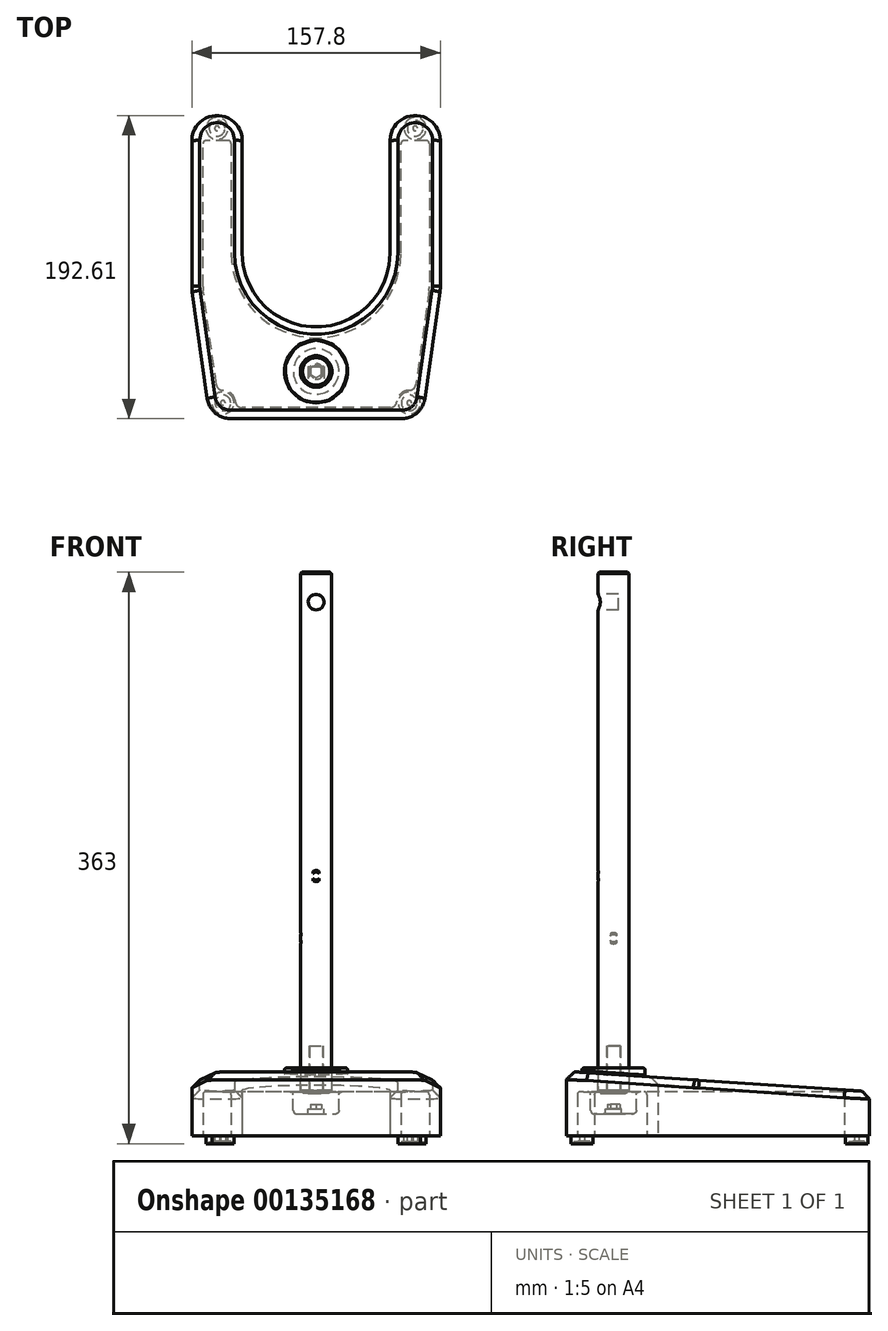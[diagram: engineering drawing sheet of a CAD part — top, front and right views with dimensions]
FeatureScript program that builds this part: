
annotation { "Feature Type Name" : "Feature", "Feature Type Description" : "" }
export const myFeature = defineFeature(function(context is Context, id is Id, definition is map)
    precondition{}
    {
        {
            var Q0;
            Q0=qCreatedBy(makeId("Top.planeOp"),FACE);
            var sketch = newSketch(context, id + "F0", { "sketchPlane" : qUnion([Q0])});
            skLineSegment(sketch, "E0", {"start": v(0, 0) * mm, "end": v(-54.3, 0) * mm});
            skLineSegment(sketch, "E1", {"start": v(-54.3, 0) * mm, "end": v(-54.3, 15) * mm, "construction": true});
            skArc(sketch, "E2", {"start": v(-69.15, 12.91) * mm, "mid": v(-64.14, 3.68) * mm, "end": v(-54.3, 0) * mm});
            skLineSegment(sketch, "E3", {"start": v(-69.15, 12.91) * mm, "end": v(-78.66, 80.53) * mm});
            skLineSegment(sketch, "E4", {"start": v(-78.9, 84) * mm, "end": v(-78.9, 176.6) * mm});
            skPoint(sketch, "E5.visualSharp", {"position": v(-78.9, 82.26) * mm});
            skArc(sketch, "E5.filletArc", {"start": v(-78.9, 84) * mm, "mid": v(-78.84, 82.26) * mm, "end": v(-78.66, 80.53) * mm});
            skLineSegment(sketch, "E6", {"start": v(-78.9, 176.6) * mm, "end": v(-62.9, 176.6) * mm, "construction": true});
            skArc(sketch, "E7", {"start": v(-46.9, 176.6) * mm, "mid": v(-62.9, 192.6) * mm, "end": v(-78.9, 176.6) * mm});
            skLineSegment(sketch, "E8", {"start": v(-46.9, 176.6) * mm, "end": v(-46.9, 105.2) * mm});
            skLineSegment(sketch, "E9", {"start": v(0, 58.3) * mm, "end": v(0, 192.6) * mm, "construction": true});
            skPoint(sketch, "E9.endSnap0", {"position": v(-62.9, 192.6) * mm});
            skArc(sketch, "E10", {"start": v(-46.9, 105.2) * mm, "mid": v(-33.16, 72.04) * mm, "end": v(0, 58.3) * mm});
            skLineSegment(sketch, "E11", {"start": v(0, 58.3) * mm, "end": v(0, 0) * mm});
            skSolve(sketch);
        }
        {
            var Q0;
            Q0=qSketchRegion(id+"F0",true);
            extrude(context, id + "F1", {"entities" : qUnion([Q0]), "depth" : 41 * mm});
        }
        {
            var Q0;
            Q0=makeQuery(id+"F1.opExtrude","SWEPT_BODY",BODY,{"disambiguationData":[OSD([sQuery(id+"F0.wireOp",EDGE,"E0"),sQuery(id+"F0.wireOp",EDGE,"E2"),sQuery(id+"F0.wireOp",EDGE,"E3"),sQuery(id+"F0.wireOp",EDGE,"E4"),sQuery(id+"F0.wireOp",EDGE,"E5.filletArc"),sQuery(id+"F0.wireOp",EDGE,"E7"),sQuery(id+"F0.wireOp",EDGE,"E8"),sQuery(id+"F0.wireOp",EDGE,"E10"),sQuery(id+"F0.wireOp",EDGE,"E11")])]});
            var Q1;
            Q1=qCreatedBy(makeId("Right.planeOp"),FACE);
            mirror(context, id + "F2", {"operationType" : NewBodyOperationType.ADD, "entities" : qUnion([Q0]), "mirrorPlane" : qUnion([Q1])});
        }
        {
            var Q0;
            Q0=qCreatedBy(makeId("Right.planeOp"),FACE);
            var sketch = newSketch(context, id + "F3", { "sketchPlane" : qUnion([Q0])});
            skLineSegment(sketch, "E12", {"start": v(0, 0) * mm, "end": v(0, 18) * mm, "construction": true});
            skPoint(sketch, "E13.0", {"position": v(0, 41) * mm});
            skLineSegment(sketch, "E14", {"start": v(0, 41) * mm, "end": v(5, 41) * mm});
            skLineSegment(sketch, "E15", {"start": v(0, 18) * mm, "end": v(192.61, 18) * mm});
            skLineSegment(sketch, "E16", {"start": v(192.61, 18) * mm, "end": v(192.61, 28) * mm, "construction": true});
            skLineSegment(sketch, "E17", {"start": v(192.61, 28) * mm, "end": v(187.6, 28) * mm});
            skLineSegment(sketch, "E18", {"start": v(192.61, 41) * mm, "end": v(192.61, 28) * mm});
            skLineSegment(sketch, "E19", {"start": v(0, 18) * mm, "end": v(0, 41) * mm});
            skLineSegment(sketch, "E20", {"start": v(5, 18) * mm, "end": v(0, 18) * mm});
            skLineSegment(sketch, "E21", {"start": v(0, 41) * mm, "end": v(192.61, 28) * mm});
            skLineSegment(sketch, "E22", {"start": v(192.61, 41) * mm, "end": v(0, 41) * mm});
            skSolve(sketch);
        }
        {
            var Q0;
            {var subQ0=sQuery(id+"F3.wireOp",EDGE,"E18");Q0=makeQuery(id+"F3.imprint","IMPRINT",FACE,{"disambiguationData":[TD([[makeQuery(id+"F3.imprint","IMPRINT",EDGE,{"derivedFrom":subQ0}),-1.0]])]});}
            extrude(context, id + "F4", {"entities" : qUnion([Q0]), "operationType" : NewBodyOperationType.REMOVE, "endBound" : BoundingType.THROUGH_ALL, "oppositeDirection" : true, "depth" : 25 * mm, "hasSecondDirection" : true, "secondDirectionBound" : SecondDirectionBoundingType.THROUGH_ALL, "secondDirectionOppositeDirection" : false, "secondDirectionDepth" : 25 * mm});
        }
        {
            var Q0;
            Q0=makeQuery(id+"F4.boolean.opBoolean","INTERSECT",EDGE,{"derivedFrom":[makeQuery(id+"F1.opExtrude","SWEPT_FACE",FACE,{"disambiguationData":[OSD([sQuery(id+"F0.wireOp",EDGE,"E4")])]}),makeQuery(id+"F4.opExtrude","SWEPT_FACE",FACE,{"disambiguationData":[OSD([sQuery(id+"F3.wireOp",EDGE,"E21")])]})]});
            chamfer(context, id + "F5", {"entities" : qUnion([Q0]), "width" : 5 * mm, "tangentPropagation" : true});
        }
        {
            var Q0;
            Q0=qCreatedBy(makeId("Front.planeOp"),FACE);
            var sketch = newSketch(context, id + "F6", { "sketchPlane" : qUnion([Q0])});
            skLineSegment(sketch, "E23", {"start": v(0, 0) * mm, "end": v(0, 44) * mm, "construction": true});
            skSolve(sketch);
        }
        {
            var Q0;
            Q0=qCreatedBy(makeId("Right.planeOp"),FACE);
            var sketch = newSketch(context, id + "F7", { "sketchPlane" : qUnion([Q0])});
            skLineSegment(sketch, "E24.0", {"start": v(0, 0) * mm, "end": v(0, 44) * mm, "construction": true});
            skLineSegment(sketch, "E25", {"start": v(0, 44) * mm, "end": v(30, 44) * mm, "construction": true});
            skSolve(sketch);
        }
        {
            var Q0;
            Q0=qCreatedBy(makeId("Top.planeOp"),FACE);
            var sketch = newSketch(context, id + "F8", { "sketchPlane" : qUnion([Q0])});
            skLineSegment(sketch, "E26.0", {"start": v(0, 0) * mm, "end": v(0, 30) * mm});
            skCircle(sketch, "E27", {"center": v(0, 30) * mm, "radius": 20 * mm});
            skSolve(sketch);
        }
        {
            var Q0;
            Q0=qSketchRegion(id+"F8",true);
            extrude(context, id + "F9", {"entities" : qUnion([Q0]), "operationType" : NewBodyOperationType.ADD, "depth" : 43 * mm});
        }
        {
            var Q0;
            Q0=makeQuery(id+"F9.opExtrude","CAP_FACE",FACE,{"disambiguationData":[OSD([sQuery(id+"F8.wireOp",EDGE,"E27")])],"isStart":false});
            var sketch = newSketch(context, id + "F10", { "sketchPlane" : qUnion([Q0])});
            skCircle(sketch, "E28", {"center": v(0, 30) * mm, "radius": 10 * mm});
            skSolve(sketch);
        }
        {
            var Q0;
            Q0=qSketchRegion(id+"F10",true);
            extrude(context, id + "F11", {"entities" : qUnion([Q0]), "operationType" : NewBodyOperationType.REMOVE, "oppositeDirection" : true, "depth" : 18 * mm});
        }
        {
            var Q0;
            Q0=makeQuery(id+"F11.boolean.opBoolean","COPY",FACE,{"derivedFrom":makeQuery(id+"F11.opExtrude","CAP_FACE",FACE,{"disambiguationData":[OSD([sQuery(id+"F10.wireOp",EDGE,"E28")])],"isStart":false})});
            var sketch = newSketch(context, id + "F12", { "sketchPlane" : qUnion([Q0])});
            skCircle(sketch, "E29", {"center": v(0, 30) * mm, "radius": 5 * mm});
            skSolve(sketch);
        }
        {
            var Q0;
            Q0=qSketchRegion(id+"F12",true);
            extrude(context, id + "F13", {"entities" : qUnion([Q0]), "operationType" : NewBodyOperationType.REMOVE, "endBound" : BoundingType.THROUGH_ALL, "oppositeDirection" : true, "depth" : 25 * mm});
        }
        {
            var Q0;
            {var subQ0=makeQuery(id+"F1.opExtrude","CAP_FACE",FACE,{"disambiguationData":[OSD([sQuery(id+"F0.wireOp",EDGE,"E0"),sQuery(id+"F0.wireOp",EDGE,"E2"),sQuery(id+"F0.wireOp",EDGE,"E3"),sQuery(id+"F0.wireOp",EDGE,"E4"),sQuery(id+"F0.wireOp",EDGE,"E5.filletArc"),sQuery(id+"F0.wireOp",EDGE,"E7"),sQuery(id+"F0.wireOp",EDGE,"E8"),sQuery(id+"F0.wireOp",EDGE,"E10"),sQuery(id+"F0.wireOp",EDGE,"E11")])],"isStart":true});Q0=makeQuery(id+"F2.boolean.opBoolean","MERGE",FACE,{"derivedFrom":[subQ0,makeQuery(id+"F2.opPattern","COPY",FACE,{"derivedFrom":subQ0,"instanceName":"1"})]});}
            var sketch = newSketch(context, id + "F14", { "sketchPlane" : qUnion([Q0])});
            skLineSegment(sketch, "E30.1", {"start": v(71.72, -81.5) * mm, "end": v(63.28, -21.44) * mm});
            skArc(sketch, "E30.2", {"start": v(71.9, -84) * mm, "mid": v(71.86, -82.75) * mm, "end": v(71.72, -81.5) * mm});
            skLineSegment(sketch, "E30.3", {"start": v(-71.9, -84) * mm, "end": v(-71.9, -174.6) * mm});
            skArc(sketch, "E30.4", {"start": v(-71.72, -81.5) * mm, "mid": v(-71.86, -82.75) * mm, "end": v(-71.9, -84) * mm});
            skLineSegment(sketch, "E30.5", {"start": v(-63, -19.44) * mm, "end": v(-71.72, -81.5) * mm});
            skLineSegment(sketch, "E30.8", {"start": v(-53.9, -174.6) * mm, "end": v(-53.9, -105.2) * mm});
            skArc(sketch, "E30.9", {"start": v(-53.9, -105.2) * mm, "mid": v(0, -51.3) * mm, "end": v(53.9, -105.2) * mm});
            skLineSegment(sketch, "E30.10", {"start": v(47.2, -7) * mm, "end": v(-47.2, -7) * mm});
            skLineSegment(sketch, "E30.11", {"start": v(53.9, -105.2) * mm, "end": v(53.9, -174.6) * mm});
            skLineSegment(sketch, "E30.13", {"start": v(71.9, -174.6) * mm, "end": v(71.9, -84) * mm});
            skLineSegment(sketch, "E31", {"start": v(69.9, -176.6) * mm, "end": v(55.9, -176.6) * mm});
            skLineSegment(sketch, "E32", {"start": v(-55.9, -176.6) * mm, "end": v(-69.9, -176.6) * mm});
            skPoint(sketch, "E33.visualSharp", {"position": v(71.9, -176.6) * mm});
            skArc(sketch, "E33.filletArc", {"start": v(69.9, -176.6) * mm, "mid": v(71.31, -176.02) * mm, "end": v(71.9, -174.6) * mm});
            skPoint(sketch, "E34.visualSharp", {"position": v(53.9, -176.6) * mm});
            skArc(sketch, "E34.filletArc", {"start": v(53.9, -174.6) * mm, "mid": v(54.49, -176.02) * mm, "end": v(55.9, -176.6) * mm});
            skPoint(sketch, "E35.visualSharp", {"position": v(-53.9, -176.6) * mm});
            skArc(sketch, "E35.filletArc", {"start": v(-55.9, -176.6) * mm, "mid": v(-54.49, -176.02) * mm, "end": v(-53.9, -174.6) * mm});
            skPoint(sketch, "E36.visualSharp", {"position": v(-71.9, -176.6) * mm});
            skArc(sketch, "E36.filletArc", {"start": v(-71.9, -174.6) * mm, "mid": v(-71.31, -176.02) * mm, "end": v(-69.9, -176.6) * mm});
            skArc(sketch, "E37", {"start": v(51.18, -10.67) * mm, "mid": v(53.78, -15.93) * mm, "end": v(59.27, -18) * mm});
            skPoint(sketch, "E38.visualSharp", {"position": v(51.74, -7) * mm});
            skArc(sketch, "E38.filletArc", {"start": v(51.18, -10.67) * mm, "mid": v(49.9, -8.06) * mm, "end": v(47.2, -7) * mm});
            skPoint(sketch, "E39.visualSharp", {"position": v(62.68, -17.18) * mm});
            skArc(sketch, "E39.filletArc", {"start": v(63.28, -21.44) * mm, "mid": v(61.93, -18.96) * mm, "end": v(59.27, -18) * mm});
            skLineSegment(sketch, "E40", {"start": v(0, 0) * mm, "end": v(0, -30) * mm, "construction": true});
            skArc(sketch, "E41.MirrorCS", {"start": v(-63.28, -21.44) * mm, "mid": v(-61.93, -18.96) * mm, "end": v(-59.27, -18) * mm});
            skArc(sketch, "E42.MirrorCS", {"start": v(-51.18, -10.67) * mm, "mid": v(-53.78, -15.93) * mm, "end": v(-59.27, -18) * mm});
            skArc(sketch, "E43.MirrorCS", {"start": v(-51.18, -10.67) * mm, "mid": v(-49.9, -8.06) * mm, "end": v(-47.2, -7) * mm});
            skSolve(sketch);
        }
        {
            var Q0;
            Q0=qSketchRegion(id+"F14",true);
            extrude(context, id + "F15", {"entities" : qUnion([Q0]), "operationType" : NewBodyOperationType.REMOVE, "oppositeDirection" : true, "depth" : 28 * mm});
        }
        {
            var Q0;
            Q0=makeQuery(id+"F15.boolean.opBoolean","COPY",FACE,{"derivedFrom":makeQuery(id+"F15.opExtrude","CAP_FACE",FACE,{"disambiguationData":[OSD([sQuery(id+"F14.wireOp",EDGE,"E30.1"),sQuery(id+"F14.wireOp",EDGE,"E30.2"),sQuery(id+"F14.wireOp",EDGE,"E30.3"),sQuery(id+"F14.wireOp",EDGE,"E30.4"),sQuery(id+"F14.wireOp",EDGE,"E30.5"),sQuery(id+"F14.wireOp",EDGE,"E30.8"),sQuery(id+"F14.wireOp",EDGE,"E30.9"),sQuery(id+"F14.wireOp",EDGE,"E30.10"),sQuery(id+"F14.wireOp",EDGE,"E30.11"),sQuery(id+"F14.wireOp",EDGE,"E30.13"),sQuery(id+"F14.wireOp",EDGE,"E31"),sQuery(id+"F14.wireOp",EDGE,"E32"),sQuery(id+"F14.wireOp",EDGE,"E33.filletArc"),sQuery(id+"F14.wireOp",EDGE,"E34.filletArc"),sQuery(id+"F14.wireOp",EDGE,"E35.filletArc"),sQuery(id+"F14.wireOp",EDGE,"E36.filletArc"),sQuery(id+"F14.wireOp",EDGE,"E37"),sQuery(id+"F14.wireOp",EDGE,"E38.filletArc"),sQuery(id+"F14.wireOp",EDGE,"E39.filletArc"),sQuery(id+"F14.wireOp",EDGE,"E41.MirrorCS"),sQuery(id+"F14.wireOp",EDGE,"E42.MirrorCS"),sQuery(id+"F14.wireOp",EDGE,"E43.MirrorCS")])],"isStart":false})});
            var sketch = newSketch(context, id + "F16", { "sketchPlane" : qUnion([Q0])});
            skCircle(sketch, "E44", {"center": v(0, -30) * mm, "radius": 14.5 * mm});
            skCircle(sketch, "E45", {"center": v(0, -30) * mm, "radius": 5 * mm});
            skSolve(sketch);
        }
        {
            var Q0;
            Q0=qSketchRegion(id+"F16",true);
            extrude(context, id + "F17", {"entities" : qUnion([Q0]), "operationType" : NewBodyOperationType.ADD, "depth" : 14 * mm});
        }
        {
            var Q0;
            {var subQ0=makeQuery(id+"F1.opExtrude","CAP_FACE",FACE,{"disambiguationData":[OSD([sQuery(id+"F0.wireOp",EDGE,"E0"),sQuery(id+"F0.wireOp",EDGE,"E2"),sQuery(id+"F0.wireOp",EDGE,"E3"),sQuery(id+"F0.wireOp",EDGE,"E4"),sQuery(id+"F0.wireOp",EDGE,"E5.filletArc"),sQuery(id+"F0.wireOp",EDGE,"E7"),sQuery(id+"F0.wireOp",EDGE,"E8"),sQuery(id+"F0.wireOp",EDGE,"E10"),sQuery(id+"F0.wireOp",EDGE,"E11")])],"isStart":true});Q0=makeQuery(id+"F2.boolean.opBoolean","MERGE",FACE,{"derivedFrom":[subQ0,makeQuery(id+"F2.opPattern","COPY",FACE,{"derivedFrom":subQ0,"instanceName":"1"})]});}
            var sketch = newSketch(context, id + "F18", { "sketchPlane" : qUnion([Q0])});
            skCircle(sketch, "E46", {"center": v(59.15, -10) * mm, "radius": 7 * mm});
            skCircle(sketch, "E47", {"center": v(62.9, -184.4) * mm, "radius": 7 * mm});
            skPoint(sketch, "E47.centerSnap0", {"position": v(62.9, -192.6) * mm});
            skSolve(sketch);
        }
        {
            var Q0;
            Q0=qSketchRegion(id+"F18",true);
            extrude(context, id + "F19", {"entities" : qUnion([Q0]), "depth" : 5 * mm});
        }
        {
            var Q0;
            Q0=makeQuery(id+"F19.opExtrude","CAP_FACE",FACE,{"disambiguationData":[OSD([sQuery(id+"F18.wireOp",EDGE,"E46")])],"isStart":false});
            var sketch = newSketch(context, id + "F20", { "sketchPlane" : qUnion([Q0])});
            skCircle(sketch, "E48", {"center": v(59.15, -10) * mm, "radius": 5 * mm});
            skSolve(sketch);
        }
        {
            var Q0;
            Q0=qSketchRegion(id+"F20",true);
            extrude(context, id + "F21", {"entities" : qUnion([Q0]), "operationType" : NewBodyOperationType.REMOVE, "oppositeDirection" : true, "depth" : 1.5 * mm});
        }
        {
            var Q0;
            Q0=makeQuery(id+"F21.boolean.opBoolean","COPY",FACE,{"derivedFrom":makeQuery(id+"F21.opExtrude","CAP_FACE",FACE,{"disambiguationData":[OSD([sQuery(id+"F20.wireOp",EDGE,"E48")])],"isStart":false})});
            var sketch = newSketch(context, id + "F22", { "sketchPlane" : qUnion([Q0])});
            skCircle(sketch, "E49.0", {"center": v(59.15, -10) * mm, "radius": 5 * mm, "construction": true});
            skCircle(sketch, "E50", {"center": v(59.15, -10) * mm, "radius": 1.5 * mm});
            skSolve(sketch);
        }
        {
            var Q0;
            Q0=makeQuery(id+"F22.imprint","IMPRINT",FACE,{"disambiguationData":[TD([[makeQuery(id+"F22.imprint","IMPRINT",EDGE,{"derivedFrom":sQuery(id+"F22.wireOp",EDGE,"E50")}),1.0]])]});
            extrude(context, id + "F23", {"entities" : qUnion([Q0]), "operationType" : NewBodyOperationType.REMOVE, "oppositeDirection" : true, "depth" : 3 * mm});
        }
        {
            var Q0;
            Q0=makeQuery(id+"F19.opExtrude","CAP_FACE",FACE,{"disambiguationData":[OSD([sQuery(id+"F18.wireOp",EDGE,"E47")])],"isStart":false});
            var sketch = newSketch(context, id + "F24", { "sketchPlane" : qUnion([Q0])});
            skCircle(sketch, "E51", {"center": v(62.9, -184.4) * mm, "radius": 5 * mm});
            skSolve(sketch);
        }
        {
            var Q0;
            Q0=qSketchRegion(id+"F24",true);
            extrude(context, id + "F25", {"entities" : qUnion([Q0]), "operationType" : NewBodyOperationType.REMOVE, "oppositeDirection" : true, "depth" : 1.5 * mm});
        }
        {
            var Q0;
            Q0=makeQuery(id+"F25.boolean.opBoolean","COPY",FACE,{"derivedFrom":makeQuery(id+"F25.opExtrude","CAP_FACE",FACE,{"disambiguationData":[OSD([sQuery(id+"F24.wireOp",EDGE,"E51")])],"isStart":false})});
            var sketch = newSketch(context, id + "F26", { "sketchPlane" : qUnion([Q0])});
            skCircle(sketch, "E52", {"center": v(62.9, -184.4) * mm, "radius": 1.5 * mm});
            skSolve(sketch);
        }
        {
            var Q0;
            Q0=qSketchRegion(id+"F26",true);
            extrude(context, id + "F27", {"entities" : qUnion([Q0]), "operationType" : NewBodyOperationType.REMOVE, "oppositeDirection" : true, "depth" : 3 * mm});
        }
        {
            var Q0;
            Q0=makeQuery(id+"F19.opExtrude","SWEPT_BODY",BODY,{"disambiguationData":[OSD([sQuery(id+"F18.wireOp",EDGE,"E46")])]});
            var Q1;
            Q1=makeQuery(id+"F19.opExtrude","SWEPT_BODY",BODY,{"disambiguationData":[OSD([sQuery(id+"F18.wireOp",EDGE,"E47")])]});
            var Q2;
            Q2=qCreatedBy(makeId("Right.planeOp"),FACE);
            mirror(context, id + "F28", {"entities" : qUnion([Q0, Q1]), "mirrorPlane" : qUnion([Q2])});
        }
        {
            var Q0;
            Q0=makeQuery(id+"F15.boolean.opBoolean","COPY",FACE,{"derivedFrom":makeQuery(id+"F15.opExtrude","CAP_FACE",FACE,{"disambiguationData":[OSD([sQuery(id+"F14.wireOp",EDGE,"E30.1"),sQuery(id+"F14.wireOp",EDGE,"E30.2"),sQuery(id+"F14.wireOp",EDGE,"E30.3"),sQuery(id+"F14.wireOp",EDGE,"E30.4"),sQuery(id+"F14.wireOp",EDGE,"E30.5"),sQuery(id+"F14.wireOp",EDGE,"E30.8"),sQuery(id+"F14.wireOp",EDGE,"E30.9"),sQuery(id+"F14.wireOp",EDGE,"E30.10"),sQuery(id+"F14.wireOp",EDGE,"E30.11"),sQuery(id+"F14.wireOp",EDGE,"E30.13"),sQuery(id+"F14.wireOp",EDGE,"E31"),sQuery(id+"F14.wireOp",EDGE,"E32"),sQuery(id+"F14.wireOp",EDGE,"E33.filletArc"),sQuery(id+"F14.wireOp",EDGE,"E34.filletArc"),sQuery(id+"F14.wireOp",EDGE,"E35.filletArc"),sQuery(id+"F14.wireOp",EDGE,"E36.filletArc"),sQuery(id+"F14.wireOp",EDGE,"E37"),sQuery(id+"F14.wireOp",EDGE,"E38.filletArc"),sQuery(id+"F14.wireOp",EDGE,"E39.filletArc"),sQuery(id+"F14.wireOp",EDGE,"E41.MirrorCS"),sQuery(id+"F14.wireOp",EDGE,"E42.MirrorCS"),sQuery(id+"F14.wireOp",EDGE,"E43.MirrorCS")])],"isStart":false})});
            var Q1;
            Q1=makeQuery(id+"F17.opExtrude","CAP_EDGE",EDGE,{"disambiguationData":[OSD([sQuery(id+"F16.wireOp",EDGE,"E44")])],"isStart":false});
            fillet(context, id + "F29", {"entities" : qUnion([Q0, Q1]), "radius" : 2 * mm, "tangentPropagation" : true, "allowEdgeOverflow" : false});
        }
        {
            var Q0;
            Q0=makeQuery(id+"F15.boolean.opBoolean","COPY",EDGE,{"derivedFrom":makeQuery(id+"F15.opExtrude","CAP_EDGE",EDGE,{"disambiguationData":[OSD([sQuery(id+"F14.wireOp",EDGE,"E30.1")])],"isStart":true})});
            var Q1;
            Q1=makeQuery(id+"F9.opExtrude","CAP_EDGE",EDGE,{"disambiguationData":[OSD([sQuery(id+"F8.wireOp",EDGE,"E27")])],"isStart":false});
            var Q2;
            Q2=makeQuery(id+"F9.boolean.opBoolean","INTERSECT",EDGE,{"derivedFrom":[makeQuery(id+"F4.boolean.opBoolean","COPY",FACE,{"derivedFrom":makeQuery(id+"F4.opExtrude","SWEPT_FACE",FACE,{"disambiguationData":[OSD([sQuery(id+"F3.wireOp",EDGE,"E21")])]})}),makeQuery(id+"F9.opExtrude","SWEPT_FACE",FACE,{"disambiguationData":[OSD([sQuery(id+"F8.wireOp",EDGE,"E27")])]})]});
            fillet(context, id + "F30", {"entities" : qUnion([Q0, Q1, Q2]), "radius" : 1 * mm, "tangentPropagation" : true, "allowEdgeOverflow" : false});
        }
        {
            var Q0;
            Q0=makeQuery(id+"F17.opExtrude","CAP_FACE",FACE,{"disambiguationData":[OSD([sQuery(id+"F16.wireOp",EDGE,"E44"),sQuery(id+"F16.wireOp",EDGE,"E45")])],"isStart":true});
            var sketch = newSketch(context, id + "F31", { "sketchPlane" : qUnion([Q0])});
            skCircle(sketch, "E53", {"center": v(0, 30) * mm, "radius": 9.8 * mm});
            skSolve(sketch);
        }
        {
            var Q0;
            Q0=qSketchRegion(id+"F31",true);
            extrude(context, id + "F32", {"entities" : qUnion([Q0]), "depth" : 330 * mm});
        }
        {
            var Q0;
            Q0=makeQuery(id+"F32.opExtrude","CAP_FACE",FACE,{"disambiguationData":[OSD([sQuery(id+"F31.wireOp",EDGE,"E53")])],"isStart":true});
            var sketch = newSketch(context, id + "F33", { "sketchPlane" : qUnion([Q0])});
            skCircle(sketch, "E54", {"center": v(0, -30) * mm, "radius": 4.3 * mm});
            skSolve(sketch);
        }
        {
            var Q0;
            Q0=qSketchRegion(id+"F33",true);
            extrude(context, id + "F34", {"entities" : qUnion([Q0]), "operationType" : NewBodyOperationType.REMOVE, "oppositeDirection" : true, "depth" : 29 * mm});
        }
        {
            var Q0;
            Q0=qCreatedBy(makeId("Front.planeOp"),FACE);
            var sketch = newSketch(context, id + "F35", { "sketchPlane" : qUnion([Q0])});
            skLineSegment(sketch, "E55.0", {"start": v(-9.8, 358) * mm, "end": v(9.8, 358) * mm, "construction": true});
            skLineSegment(sketch, "E56", {"start": v(0, 358) * mm, "end": v(0, 339) * mm, "construction": true});
            skPoint(sketch, "E56.endSnap0", {"position": v(0, 358) * mm});
            skCircle(sketch, "E57", {"center": v(0, 339) * mm, "radius": 5 * mm});
            skLineSegment(sketch, "E58", {"start": v(0, 334) * mm, "end": v(0, 165) * mm, "construction": true});
            skCircle(sketch, "E59", {"center": v(0, 165) * mm, "radius": 3.5 * mm});
            skCircle(sketch, "E60", {"center": v(0, 165) * mm, "radius": 2.5 * mm});
            skLineSegment(sketch, "E61", {"start": v(-9.8, 28) * mm, "end": v(-9.8, 358) * mm, "construction": true});
            skLineSegment(sketch, "E62", {"start": v(0, 168.5) * mm, "end": v(-9.8, 168.5) * mm, "construction": true});
            skSolve(sketch);
        }
        {
            var Q0;
            Q0=makeQuery(id+"F35.imprint","IMPRINT",FACE,{"disambiguationData":[TD([[makeQuery(id+"F35.imprint","IMPRINT",EDGE,{"derivedFrom":sQuery(id+"F35.wireOp",EDGE,"E57")}),1.0]])]});
            extrude(context, id + "F36", {"entities" : qUnion([Q0]), "operationType" : NewBodyOperationType.REMOVE, "oppositeDirection" : true, "depth" : 33 * mm});
        }
        {
            var Q0;
            Q0=makeQuery(id+"F32.opExtrude","CAP_FACE",FACE,{"disambiguationData":[OSD([sQuery(id+"F31.wireOp",EDGE,"E53")])],"isStart":true});
            var sketch = newSketch(context, id + "F37", { "sketchPlane" : qUnion([Q0])});
            skCircle(sketch, "E63.0", {"center": v(0, -30) * mm, "radius": 4.3 * mm});
            skSolve(sketch);
        }
        {
            var Q0;
            Q0=qSketchRegion(id+"F37",true);
            extrude(context, id + "F38", {"entities" : qUnion([Q0]), "depth" : 1 * mm, "hasSecondDirection" : true, "secondDirectionOppositeDirection" : true, "secondDirectionDepth" : 29 * mm});
        }
        {
            var Q0;
            Q0=makeQuery(id+"F38.opExtrude","CAP_FACE",FACE,{"disambiguationData":[OSD([sQuery(id+"F37.wireOp",EDGE,"E63.0")])],"isStart":false});
            var sketch = newSketch(context, id + "F39", { "sketchPlane" : qUnion([Q0])});
            skCircle(sketch, "E64", {"center": v(0, -30) * mm, "radius": 5.5 * mm});
            skSolve(sketch);
        }
        {
            var Q0;
            Q0=qSketchRegion(id+"F39",true);
            extrude(context, id + "F40", {"entities" : qUnion([Q0]), "operationType" : NewBodyOperationType.ADD, "depth" : 10 * mm});
        }
        {
            var Q0;
            Q0=makeQuery(id+"F40.opExtrude","CAP_FACE",FACE,{"disambiguationData":[OSD([sQuery(id+"F39.wireOp",EDGE,"E64")])],"isStart":true});
            var sketch = newSketch(context, id + "F41", { "sketchPlane" : qUnion([Q0])});
            skCircle(sketch, "E65", {"center": v(0, 30) * mm, "radius": 8.25 * mm});
            skCircle(sketch, "E66", {"center": v(0, 30) * mm, "radius": 5 * mm});
            skSolve(sketch);
        }
        {
            var Q0;
            Q0=qSketchRegion(id+"F41",true);
            extrude(context, id + "F42", {"entities" : qUnion([Q0]), "depth" : 2 * mm});
        }
        {
            var Q0;
            Q0=makeQuery(id+"F40.opExtrude","CAP_FACE",FACE,{"disambiguationData":[OSD([sQuery(id+"F39.wireOp",EDGE,"E64")])],"isStart":false});
            var sketch = newSketch(context, id + "F43", { "sketchPlane" : qUnion([Q0])});
            skCircle(sketch, "E67.cCircle", {"center": v(0, -30) * mm, "radius": 4 * mm, "construction": true});
            skLineSegment(sketch, "E67.0", {"start": v(0, -26) * mm, "end": v(3.46, -28) * mm});
            skLineSegment(sketch, "E67.1", {"start": v(3.46, -28) * mm, "end": v(3.46, -32) * mm});
            skLineSegment(sketch, "E67.2", {"start": v(3.46, -32) * mm, "end": v(0, -34) * mm});
            skLineSegment(sketch, "E67.3", {"start": v(0, -34) * mm, "end": v(-3.46, -32) * mm});
            skLineSegment(sketch, "E67.4", {"start": v(-3.46, -32) * mm, "end": v(-3.46, -28) * mm});
            skLineSegment(sketch, "E67.5", {"start": v(-3.46, -28) * mm, "end": v(0, -26) * mm});
            skSolve(sketch);
        }
        {
            var Q0;
            Q0=qSketchRegion(id+"F43",true);
            extrude(context, id + "F44", {"entities" : qUnion([Q0]), "operationType" : NewBodyOperationType.REMOVE, "oppositeDirection" : true, "depth" : 3 * mm});
        }
        {
            var Q0;
            Q0=makeQuery(id+"F35.imprint","IMPRINT",FACE,{"disambiguationData":[TD([[makeQuery(id+"F35.imprint","IMPRINT",EDGE,{"derivedFrom":sQuery(id+"F35.wireOp",EDGE,"E59")}),1.0]])]});
            extrude(context, id + "F45", {"entities" : qUnion([Q0]), "operationType" : NewBodyOperationType.REMOVE, "oppositeDirection" : true, "depth" : 20.4 * mm});
        }
        {
            var Q0;
            Q0=qCreatedBy(makeId("Right.planeOp"),FACE);
            var sketch = newSketch(context, id + "F46", { "sketchPlane" : qUnion([Q0])});
            skLineSegment(sketch, "E68.0", {"start": v(20.2, 358) * mm, "end": v(39.8, 358) * mm, "construction": true});
            skLineSegment(sketch, "E69", {"start": v(0, 168.5) * mm, "end": v(30, 168.5) * mm, "construction": true});
            skPoint(sketch, "E69.endSnap0", {"position": v(30, 358) * mm});
            skLineSegment(sketch, "E70", {"start": v(30, 168.5) * mm, "end": v(30, 125.5) * mm, "construction": true});
            skCircle(sketch, "E71", {"center": v(30, 125.5) * mm, "radius": 3.5 * mm, "construction": true});
            skCircle(sketch, "E72", {"center": v(30, 125.5) * mm, "radius": 2.5 * mm, "construction": true});
            skSolve(sketch);
        }
        {
            var Q0;
            Q0=qCreatedBy(makeId("Right.planeOp"),FACE);
            cPlane(context, id + "F47", {"entities" : qUnion([Q0]), "cplaneType" : CPlaneType.OFFSET, "offset" : 9.8 * mm, "oppositeDirection" : true, "width" : 150 * mm, "height" : 150 * mm});
        }
        {
            var Q0;
            Q0=qCreatedBy(id+"F47.planeOp",FACE);
            var sketch = newSketch(context, id + "F48", { "sketchPlane" : qUnion([Q0])});
            skCircle(sketch, "E73.0", {"center": v(30, 125.5) * mm, "radius": 3.5 * mm});
            skCircle(sketch, "E74.0", {"center": v(30, 125.5) * mm, "radius": 2.5 * mm});
            skSolve(sketch);
        }
        {
            var Q0;
            Q0=qSketchRegion(id+"F48",true);
            extrude(context, id + "F49", {"entities" : qUnion([Q0]), "operationType" : NewBodyOperationType.REMOVE, "depth" : 0.2 * mm});
        }
        {
            var Q0;
            Q0=makeQuery(id+"F32.opExtrude","CAP_EDGE",EDGE,{"disambiguationData":[OSD([sQuery(id+"F31.wireOp",EDGE,"E53")])],"isStart":false});
            var Q1;
            Q1=makeQuery(id+"F32.opExtrude","CAP_EDGE",EDGE,{"disambiguationData":[OSD([sQuery(id+"F31.wireOp",EDGE,"E53")])],"isStart":true});
            chamfer(context, id + "F50", {"entities" : qUnion([Q0, Q1]), "width" : 1 * mm, "tangentPropagation" : true});
        }
    });
